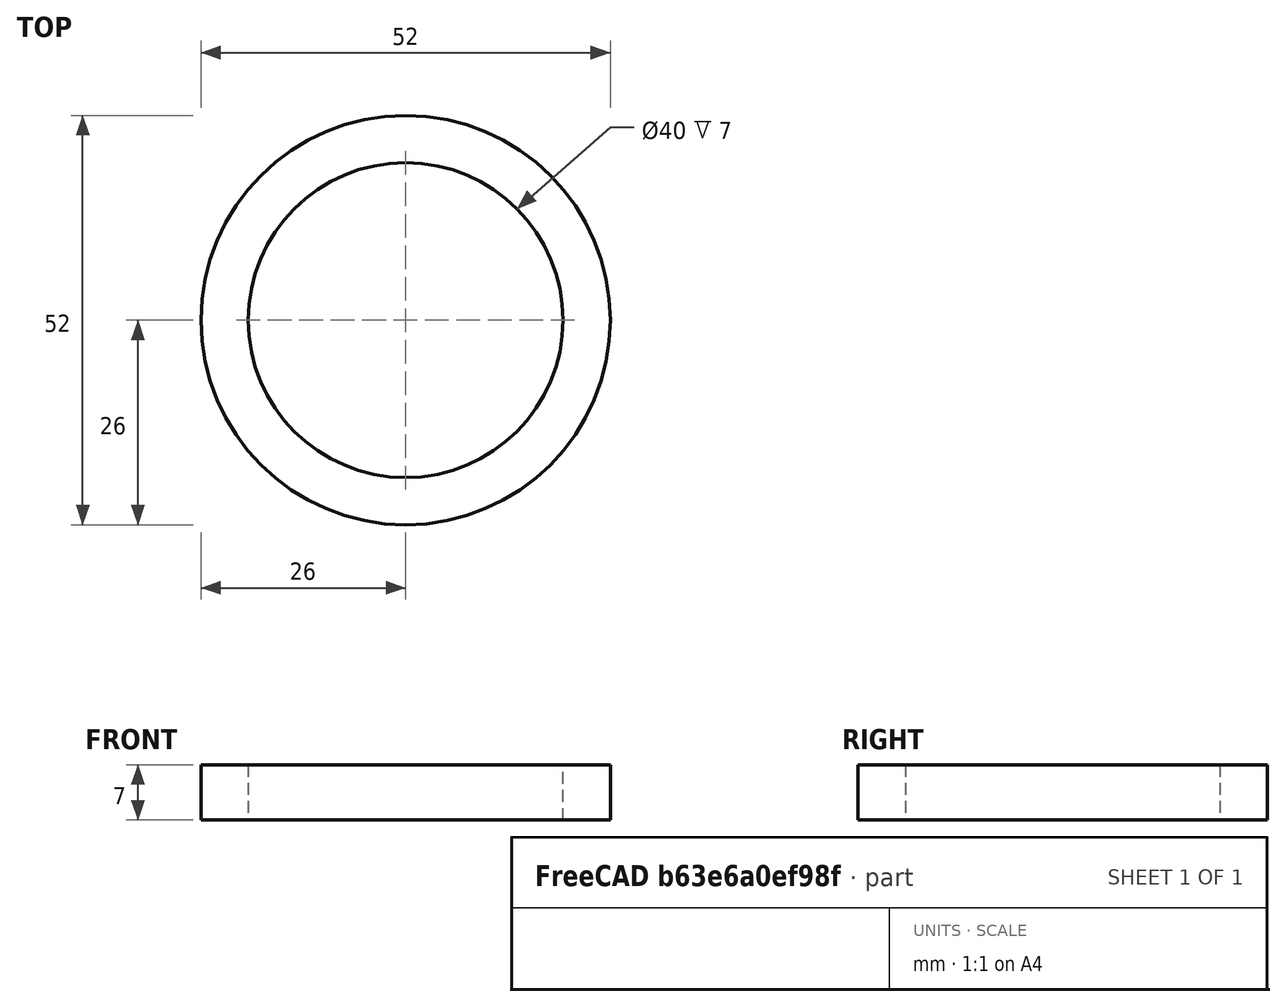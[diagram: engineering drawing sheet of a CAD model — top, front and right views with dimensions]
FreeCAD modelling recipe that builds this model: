
FCSTD DOCUMENT  (FreeCAD 0.19R24276 (Git))
Label: BALL-6808
License: All rights reserved
LicenseURL: http://en.wikipedia.org/wiki/All_rights_reserved
objects: Sketcher::SketchObject×1, PartDesign::Pad×1, PartDesign::Body×1, PartDesign::CoordinateSystem×1, App::Part×1
note: 5 computed .brp shape members not serialized (recipe doc carries the construction recipe); baked Part::Feature solids carry a one-line shape summary decoded from their .brp

FEATURE [Sketcher::SketchObject] Sketch
  FullyConstrained = true
  MapMode = 5
  Support = -> [XY_Plane]
  sketch-geometry (2):
    g0: Circle CenterX=0 CenterY=0 CenterZ=0 NormalX=0 NormalY=0 NormalZ=1 AngleXU=0 Radius=20
    g1: Circle CenterX=0 CenterY=0 CenterZ=0 NormalX=0 NormalY=0 NormalZ=1 AngleXU=0 Radius=26
  constraints (4):
    c: Coincident(g0,g-1)
    c: Coincident(g1,g0)
    c: Diameter(g0) = 40
    c: Diameter(g1) = 52
FEATURE [PartDesign::Pad] Pad
  Direction = (1,1,1)
  Length = 7
  Length2 = 100
  Profile = -> Sketch
  Refine = true
  Type = 0
FEATURE [PartDesign::Body] Body
  Group = -> [Sketch,Pad]
  Origin = -> Origin
  Tip = -> Pad
FEATURE [PartDesign::CoordinateSystem] LCS_0
  AttacherType = Attacher::AttachEngine3D
  MapMode = 2
  Support = -> [X_Axis001]
FEATURE [App::Part] Part
  Group = -> [LCS_0,Body]
  Origin = -> Origin001
